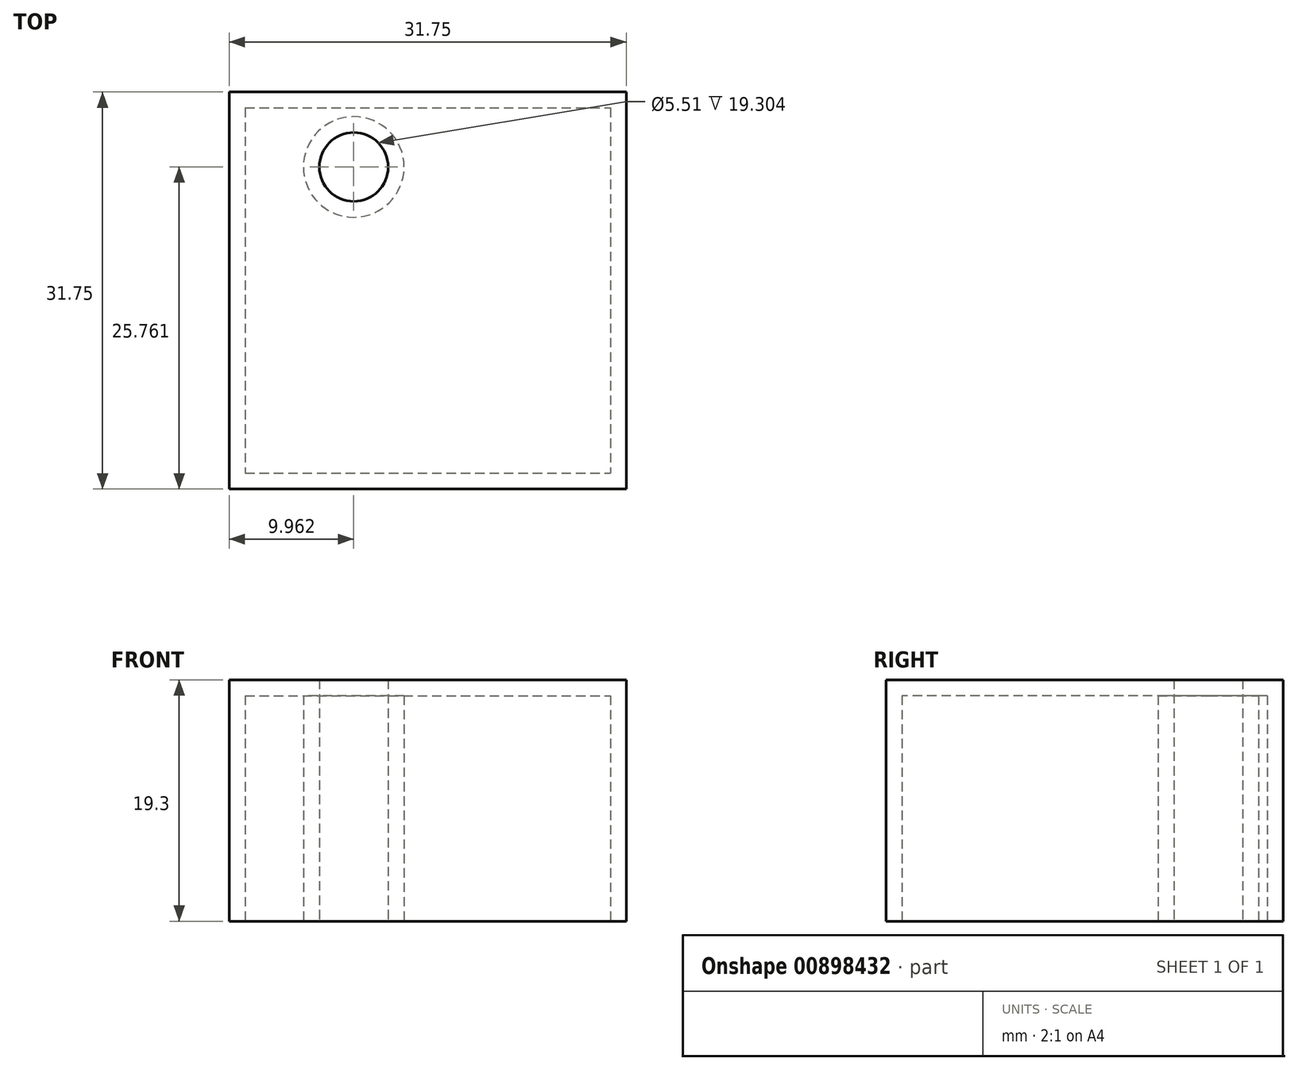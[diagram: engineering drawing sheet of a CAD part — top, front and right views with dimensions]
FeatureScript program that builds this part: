
annotation { "Feature Type Name" : "Feature", "Feature Type Description" : "" }
export const myFeature = defineFeature(function(context is Context, id is Id, definition is map)
    precondition{}
    {
        {
            var Q0;
            Q0=qCreatedBy(makeId("Top.planeOp"),FACE);
            var sketch = newSketch(context, id + "F0", { "sketchPlane" : qUnion([Q0])});
            skLineSegment(sketch, "E0.bottom", {"start": v(-50.92, 42.1) * mm, "end": v(-19.17, 42.1) * mm});
            skLineSegment(sketch, "E0.top", {"start": v(-50.92, 10.34) * mm, "end": v(-19.17, 10.34) * mm});
            skLineSegment(sketch, "E0.left", {"start": v(-50.92, 42.1) * mm, "end": v(-50.92, 10.34) * mm});
            skLineSegment(sketch, "E0.right", {"start": v(-19.17, 42.1) * mm, "end": v(-19.17, 10.34) * mm});
            skCircle(sketch, "E1", {"center": v(-40.96, 36.1) * mm, "radius": 2.08 * mm});
            skCircle(sketch, "E2", {"center": v(-40.96, 36.1) * mm, "radius": 2.75 * mm});
            skSolve(sketch);
        }
        {
            var Q0;
            Q0=makeQuery(id+"F0.imprint","IMPRINT",FACE,{"disambiguationData":[TD([[makeQuery(id+"F0.imprint","IMPRINT",EDGE,{"derivedFrom":sQuery(id+"F0.wireOp",EDGE,"E0.bottom")}),-1.0]])]});
            extrude(context, id + "F1", {"entities" : qUnion([Q0]), "depth" : 19.3 * mm, "offsetDistance" : 25.4 * mm});
        }
        {
            var Q0;
            Q0=makeQuery(id+"F1.opExtrude","CAP_FACE",FACE,{"disambiguationData":[OSD([sQuery(id+"F0.wireOp",EDGE,"E0.bottom"),sQuery(id+"F0.wireOp",EDGE,"E0.top"),sQuery(id+"F0.wireOp",EDGE,"E0.left"),sQuery(id+"F0.wireOp",EDGE,"E0.right")])],"isStart":true});
            shell(context, id + "F2", {"entities" : qUnion([Q0]), "thickness" : 1.27 * mm});
        }
    });
